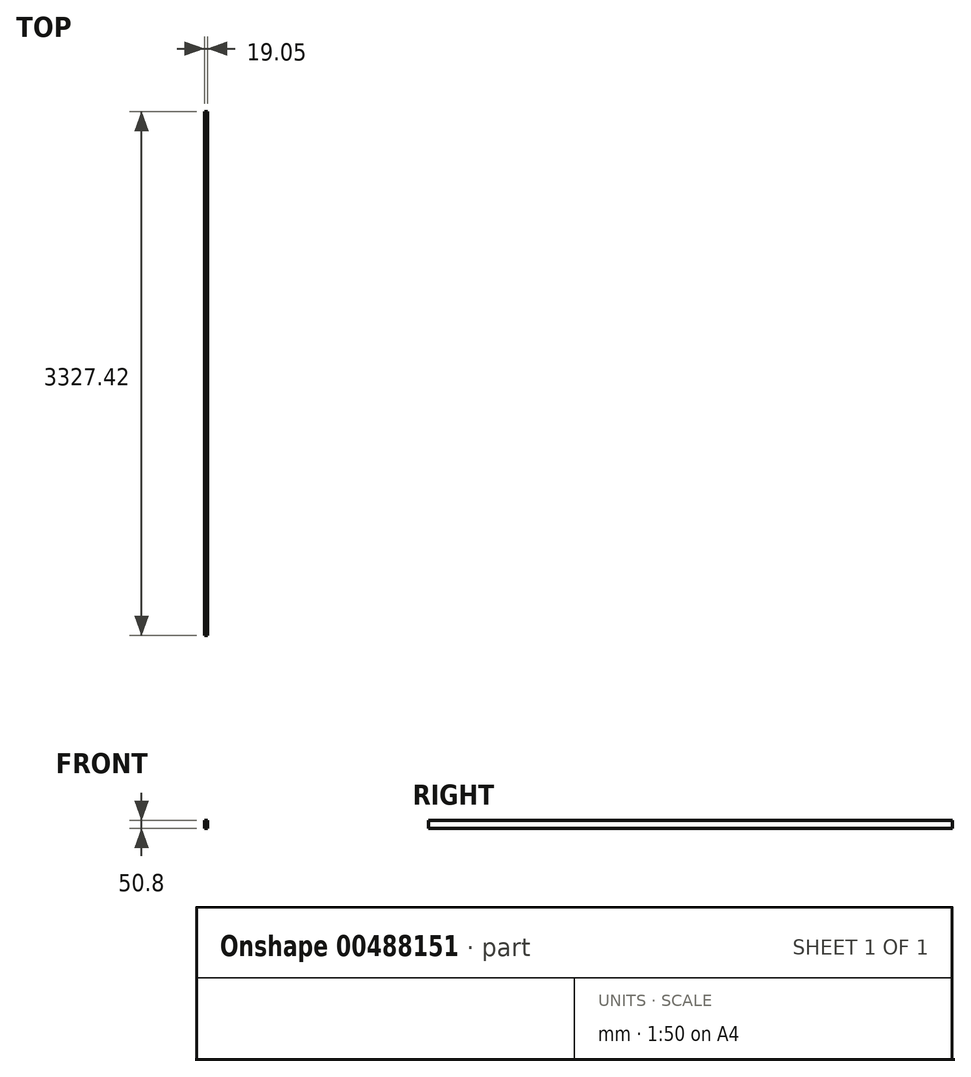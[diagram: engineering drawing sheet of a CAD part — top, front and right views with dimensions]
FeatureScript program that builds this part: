
annotation { "Feature Type Name" : "Feature", "Feature Type Description" : "" }
export const myFeature = defineFeature(function(context is Context, id is Id, definition is map)
    precondition{}
    {
        {
            var Q0;
            Q0=qCreatedBy(makeId("Front.planeOp"),FACE);
            var sketch = newSketch(context, id + "F0", { "sketchPlane" : qUnion([Q0])});
            skLineSegment(sketch, "E0", {"start": v(0, 0) * mm, "end": v(19.05, 0) * mm});
            skLineSegment(sketch, "E1", {"start": v(0, 0) * mm, "end": v(0, -50.8) * mm});
            skLineSegment(sketch, "E2", {"start": v(0, -50.8) * mm, "end": v(19.05, -50.8) * mm});
            skLineSegment(sketch, "E3", {"start": v(19.05, -50.8) * mm, "end": v(19.05, 0) * mm});
            skSolve(sketch);
        }
        {
            var Q0;
            Q0=makeQuery(id+"F0.imprint","IMPRINT",FACE,{"disambiguationData":[TD([[makeQuery(id+"F0.imprint","IMPRINT",EDGE,{"derivedFrom":sQuery(id+"F0.wireOp",EDGE,"E0")}),-1.0]])]});
            extrude(context, id + "F1", {"entities" : qUnion([Q0]), "oppositeDirection" : true, "depth" : 3048 * mm + 279.4 * mm + 5 / 203.2 * mm, "offsetDistance" : 25.4 * mm});
        }
    });
